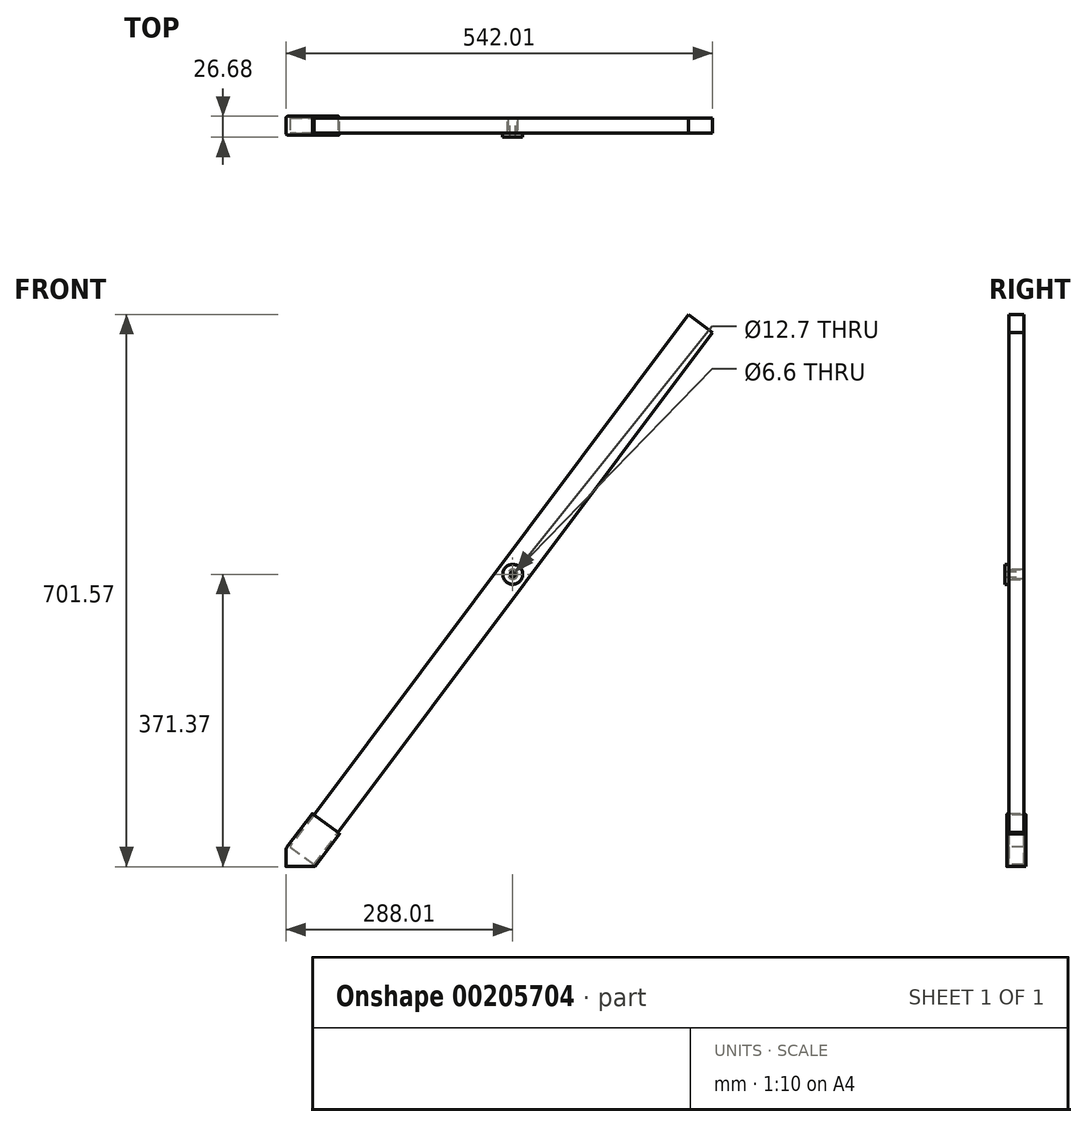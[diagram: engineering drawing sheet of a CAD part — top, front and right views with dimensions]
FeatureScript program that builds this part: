
annotation { "Feature Type Name" : "Feature", "Feature Type Description" : "" }
export const myFeature = defineFeature(function(context is Context, id is Id, definition is map)
    precondition{}
    {
        {
            var Q0;
            Q0=qCreatedBy(makeId("Front.planeOp"),FACE);
            var sketch = newSketch(context, id + "F0", { "sketchPlane" : qUnion([Q0])});
            skLineSegment(sketch, "E0", {"start": v(-223.5, 0) * mm, "end": v(-254, 22.84) * mm});
            skLineSegment(sketch, "E1", {"start": v(-254, 22.84) * mm, "end": v(223.5, 660.4) * mm});
            skLineSegment(sketch, "E2", {"start": v(223.5, 660.4) * mm, "end": v(254, 637.56) * mm});
            skLineSegment(sketch, "E3", {"start": v(-223.5, 0) * mm, "end": v(254, 637.56) * mm});
            skLineSegment(sketch, "E4", {"start": v(-238.75, 11.42) * mm, "end": v(238.75, 648.98) * mm, "construction": true});
            skPoint(sketch, "E5", {"position": v(0, 330.2) * mm});
            skCircle(sketch, "E6", {"center": v(0, 330.2) * mm, "radius": 6.35 * mm});
            skSolve(sketch);
        }
        {
            var Q0;
            Q0=qCreatedBy(makeId("Front.planeOp"),FACE);
            var sketch = newSketch(context, id + "F1", { "sketchPlane" : qUnion([Q0])});
            skLineSegment(sketch, "E7", {"start": v(-251.16, -41.17) * mm, "end": v(-288, -41.17) * mm});
            skLineSegment(sketch, "E8", {"start": v(-288, -41.17) * mm, "end": v(-288, -18.33) * mm});
            skLineSegment(sketch, "E9", {"start": v(-288, -18.33) * mm, "end": v(-254.51, 26.4) * mm});
            skLineSegment(sketch, "E10", {"start": v(-254.51, 26.4) * mm, "end": v(-219.95, 0.51) * mm});
            skLineSegment(sketch, "E11", {"start": v(-252.48, 24.87) * mm, "end": v(-282.93, -15.79) * mm});
            skLineSegment(sketch, "E12", {"start": v(-282.93, -15.79) * mm, "end": v(-252.43, -38.63) * mm});
            skLineSegment(sketch, "E13", {"start": v(-252.43, -38.63) * mm, "end": v(-221.98, 2.03) * mm});
            skLineSegment(sketch, "E14", {"start": v(-219.95, 0.51) * mm, "end": v(-251.16, -41.17) * mm});
            skSolve(sketch);
        }
        {
            var Q0;
            Q0=makeQuery(id+"F0.imprint","IMPRINT",FACE,{"disambiguationData":[TD([[makeQuery(id+"F0.imprint","IMPRINT",EDGE,{"derivedFrom":sQuery(id+"F0.wireOp",EDGE,"E0")}),-1.0]])]});
            extrude(context, id + "F2", {"entities" : qUnion([Q0]), "endBound" : BoundingType.SYMMETRIC, "depth" : 19.05 * mm});
        }
        {
            var Q0;
            Q0=makeQuery(id+"F1.imprint","IMPRINT",FACE,{"disambiguationData":[TD([[makeQuery(id+"F1.imprint","IMPRINT",EDGE,{"derivedFrom":sQuery(id+"F1.wireOp",EDGE,"E7")}),-1.0]])]});
            var Q1;
            {var subQ0=sQuery(id+"F1.wireOp",EDGE,"E11");Q1=makeQuery(id+"F1.imprint","IMPRINT",FACE,{"disambiguationData":[TD([[makeQuery(id+"F1.imprint","IMPRINT",EDGE,{"derivedFrom":subQ0}),1.0]])]});}
            extrude(context, id + "F3", {"entities" : qUnion([Q0, Q1]), "endBound" : BoundingType.SYMMETRIC, "depth" : 24.13 * mm});
        }
        {
            var Q0;
            {var subQ0=sQuery(id+"F1.wireOp",EDGE,"E11");Q0=makeQuery(id+"F1.imprint","IMPRINT",FACE,{"disambiguationData":[TD([[makeQuery(id+"F1.imprint","IMPRINT",EDGE,{"derivedFrom":subQ0}),1.0]])]});}
            extrude(context, id + "F4", {"entities" : qUnion([Q0]), "operationType" : NewBodyOperationType.REMOVE, "endBound" : BoundingType.SYMMETRIC, "oppositeDirection" : true, "depth" : 19.05 * mm});
        }
        {
            var Q0;
            Q0=makeQuery(id+"F2.opExtrude","CAP_FACE",FACE,{"disambiguationData":[OSD([sQuery(id+"F0.wireOp",EDGE,"E0"),sQuery(id+"F0.wireOp",EDGE,"E1"),sQuery(id+"F0.wireOp",EDGE,"E2"),sQuery(id+"F0.wireOp",EDGE,"E3"),sQuery(id+"F0.wireOp",EDGE,"E6")])],"isStart":false});
            var sketch = newSketch(context, id + "F5", { "sketchPlane" : qUnion([Q0])});
            skCircle(sketch, "E15.0", {"center": v(0, 330.2) * mm, "radius": 6.1 * mm});
            skLineSegment(sketch, "E16.0", {"start": v(-245.11, 24.12) * mm, "end": v(-224.78, 8.89) * mm});
            skLineSegment(sketch, "E16.1", {"start": v(224.78, 651.51) * mm, "end": v(-245.11, 24.12) * mm});
            skLineSegment(sketch, "E16.2", {"start": v(245.11, 636.28) * mm, "end": v(224.78, 651.51) * mm});
            skLineSegment(sketch, "E16.3", {"start": v(-224.78, 8.89) * mm, "end": v(245.11, 636.28) * mm});
            skCircle(sketch, "E17", {"center": v(0, 330.2) * mm, "radius": 3.3 * mm});
            skCircle(sketch, "E18", {"center": v(0, 330.2) * mm, "radius": 12.7 * mm});
            skSolve(sketch);
        }
        {
            var Q0;
            Q0=makeQuery(id+"F5.imprint","IMPRINT",FACE,{"disambiguationData":[TD([[makeQuery(id+"F5.imprint","IMPRINT",EDGE,{"derivedFrom":makeQuery(id+"F2.opExtrude","CAP_EDGE",EDGE,{"disambiguationData":[OSD([sQuery(id+"F0.wireOp",EDGE,"E6")])],"isStart":false})}),-1.0]])]});
            var Q1;
            Q1=makeQuery(id+"F5.imprint","IMPRINT",FACE,{"disambiguationData":[TD([[makeQuery(id+"F5.imprint","IMPRINT",EDGE,{"derivedFrom":sQuery(id+"F5.wireOp",EDGE,"E15.0")}),1.0]])]});
            var Q2;
            Q2=makeQuery(id+"F5.imprint","IMPRINT",FACE,{"disambiguationData":[TD([[makeQuery(id+"F5.imprint","IMPRINT",EDGE,{"derivedFrom":sQuery(id+"F5.wireOp",EDGE,"E15.0")}),-1.0]])]});
            extrude(context, id + "F6", {"entities" : qUnion([Q0, Q1, Q2]), "depth" : 5.08 * mm});
        }
        {
            var Q0;
            Q0=makeQuery(id+"F5.imprint","IMPRINT",FACE,{"disambiguationData":[TD([[makeQuery(id+"F5.imprint","IMPRINT",EDGE,{"derivedFrom":sQuery(id+"F5.wireOp",EDGE,"E15.0")}),1.0]])]});
            extrude(context, id + "F7", {"entities" : qUnion([Q0]), "operationType" : NewBodyOperationType.ADD, "oppositeDirection" : true, "depth" : 19.3 * mm});
        }
        {
            var Q0;
            Q0=makeQuery(id+"F3.opExtrude","SWEPT_EDGE",EDGE,{"disambiguationData":[OSD([sQuery(id+"F1.wireOp",EDGE,"E8"),sQuery(id+"F1.wireOp",EDGE,"E9")])]});
            fillet(context, id + "F8", {"entities" : qUnion([Q0]), "radius" : 5.08 * mm, "tangentPropagation" : true, "allowEdgeOverflow" : false});
        }
        {
            var Q0;
            Q0=makeQuery(id+"F3.opExtrude","CAP_EDGE",EDGE,{"disambiguationData":[OSD([sQuery(id+"F1.wireOp",EDGE,"E9")])],"isStart":false});
            var Q1;
            Q1=makeQuery(id+"F3.opExtrude","CAP_EDGE",EDGE,{"disambiguationData":[OSD([sQuery(id+"F1.wireOp",EDGE,"E14")])],"isStart":false});
            var Q2;
            Q2=makeQuery(id+"F3.opExtrude","CAP_EDGE",EDGE,{"disambiguationData":[OSD([sQuery(id+"F1.wireOp",EDGE,"E14")])],"isStart":true});
            var Q3;
            Q3=makeQuery(id+"F3.opExtrude","CAP_EDGE",EDGE,{"disambiguationData":[OSD([sQuery(id+"F1.wireOp",EDGE,"E9")])],"isStart":true});
            fillet(context, id + "F9", {"entities" : qUnion([Q0, Q1, Q2, Q3]), "radius" : 2.54 * mm, "tangentPropagation" : true, "allowEdgeOverflow" : false});
        }
    });
